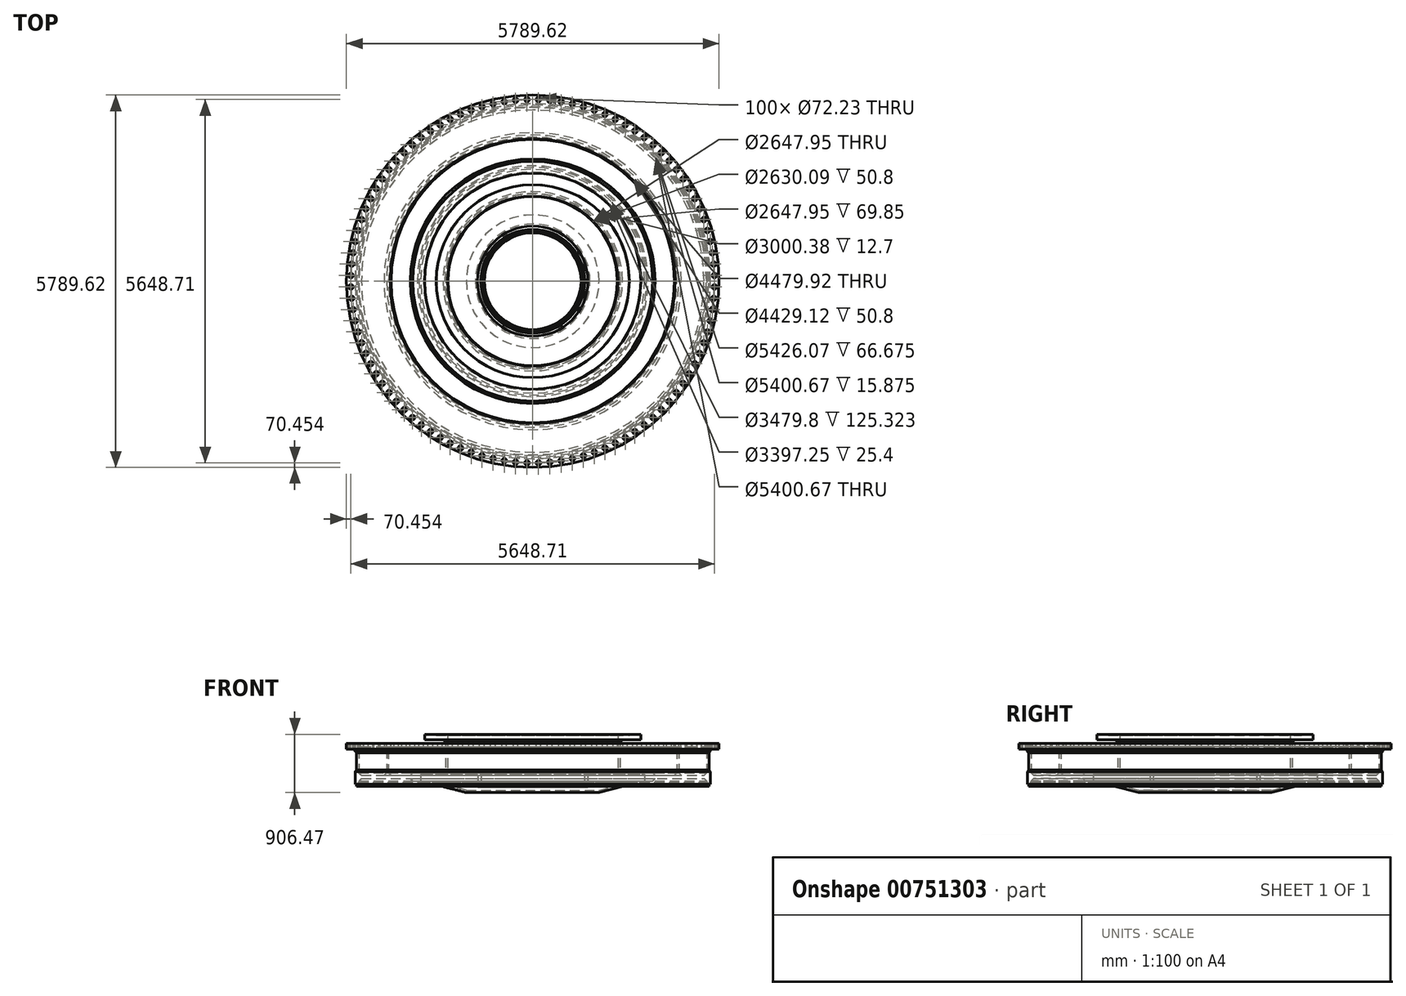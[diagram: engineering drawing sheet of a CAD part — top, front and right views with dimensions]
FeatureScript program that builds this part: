
annotation { "Feature Type Name" : "Feature", "Feature Type Description" : "" }
export const myFeature = defineFeature(function(context is Context, id is Id, definition is map)
    precondition{}
    {
        {
            var Q0;
            Q0=qCreatedBy(makeId("Front.planeOp"),FACE);
            var sketch = newSketch(context, id + "F0", { "sketchPlane" : qUnion([Q0])});
            skLineSegment(sketch, "E0", {"start": v(-1031.08, 176.21) * mm, "end": v(-1498.6, 296.47) * mm});
            skLineSegment(sketch, "E1", {"start": v(-1031.08, 212.27) * mm, "end": v(-1489.9, 330.29) * mm});
            skLineSegment(sketch, "E2", {"start": v(-1498.6, 296.47) * mm, "end": v(-1489.9, 330.29) * mm});
            skLineSegment(sketch, "E3", {"start": v(-751.28, 261.94) * mm, "end": v(-852.49, 261.94) * mm});
            skLineSegment(sketch, "E4", {"start": v(-852.49, 261.94) * mm, "end": v(-852.49, 442.91) * mm});
            skLineSegment(sketch, "E5", {"start": v(-852.49, 442.91) * mm, "end": v(-890.59, 481.01) * mm});
            skLineSegment(sketch, "E6", {"start": v(-890.59, 481.01) * mm, "end": v(-1698.62, 481.01) * mm});
            skLineSegment(sketch, "E7", {"start": v(-751.28, 261.94) * mm, "end": v(-751.28, 325.44) * mm});
            skLineSegment(sketch, "E8", {"start": v(-801.69, 357.19) * mm, "end": v(-801.69, 468.31) * mm});
            skLineSegment(sketch, "E9", {"start": v(-801.69, 468.31) * mm, "end": v(-795.34, 468.31) * mm});
            skLineSegment(sketch, "E10", {"start": v(-795.34, 468.31) * mm, "end": v(-795.34, 493.71) * mm});
            skLineSegment(sketch, "E11", {"start": v(-795.34, 493.71) * mm, "end": v(-808.04, 506.41) * mm});
            skLineSegment(sketch, "E12", {"start": v(-808.04, 506.41) * mm, "end": v(-857.25, 506.41) * mm});
            skLineSegment(sketch, "E13", {"start": v(-857.25, 506.41) * mm, "end": v(-857.25, 519.11) * mm});
            skLineSegment(sketch, "E14", {"start": v(-857.25, 519.11) * mm, "end": v(-1315.05, 519.11) * mm});
            skLineSegment(sketch, "E15", {"start": v(-1031.08, 176.21) * mm, "end": v(-1031.08, 212.27) * mm});
            skLineSegment(sketch, "E16", {"start": v(-751.28, 325.44) * mm, "end": v(-769.94, 325.44) * mm});
            skLineSegment(sketch, "E17", {"start": v(-769.94, 325.44) * mm, "end": v(-801.69, 357.19) * mm});
            skLineSegment(sketch, "E18", {"start": v(-1315.05, 519.11) * mm, "end": v(-1323.98, 528.04) * mm});
            skLineSegment(sketch, "E19", {"start": v(-1323.98, 528.04) * mm, "end": v(-1323.98, 940.4) * mm});
            skLineSegment(sketch, "E20", {"start": v(-1323.98, 940.4) * mm, "end": v(-1315.05, 949.33) * mm});
            skLineSegment(sketch, "E21", {"start": v(-1315.05, 949.33) * mm, "end": v(-1315.05, 1000.13) * mm});
            skLineSegment(sketch, "E22", {"start": v(-1315.05, 1000.13) * mm, "end": v(-1323.98, 1000.13) * mm});
            skLineSegment(sketch, "E23", {"start": v(-1323.98, 1000.13) * mm, "end": v(-1323.98, 1069.98) * mm});
            skLineSegment(sketch, "E24", {"start": v(-1323.98, 1069.98) * mm, "end": v(-1500.19, 1069.98) * mm});
            skLineSegment(sketch, "E25", {"start": v(-1500.19, 1069.98) * mm, "end": v(-1500.19, 1082.68) * mm});
            skLineSegment(sketch, "E26", {"start": v(-1500.19, 1082.68) * mm, "end": v(-1679.58, 1082.68) * mm});
            skLineSegment(sketch, "E27", {"start": v(-1679.58, 1082.68) * mm, "end": v(-1679.58, 1000.12) * mm});
            skLineSegment(sketch, "E28", {"start": v(-1679.58, 1000.13) * mm, "end": v(-2214.56, 892.18) * mm, "construction": true});
            skLineSegment(sketch, "E29", {"start": v(-2214.56, 892.18) * mm, "end": v(-2214.56, 942.97) * mm});
            skLineSegment(sketch, "E30", {"start": v(-2214.56, 942.98) * mm, "end": v(-2894.8, 942.98) * mm});
            skLineSegment(sketch, "E31", {"start": v(-2894.8, 942.97) * mm, "end": v(-2894.8, 854.07) * mm});
            skLineSegment(sketch, "E32", {"start": v(-2763.44, 822.32) * mm, "end": v(-2738.44, 797.32) * mm});
            skLineSegment(sketch, "E33", {"start": v(-2738.44, 797.32) * mm, "end": v(-2738.44, 525.46) * mm});
            skLineSegment(sketch, "E34", {"start": v(-2738.44, 525.46) * mm, "end": v(-2759.87, 504.03) * mm});
            skLineSegment(sketch, "E35", {"start": v(-2759.87, 504.03) * mm, "end": v(-2759.87, 304) * mm});
            skLineSegment(sketch, "E36", {"start": v(-2759.87, 304) * mm, "end": v(-2738.44, 304) * mm});
            skLineSegment(sketch, "E37", {"start": v(-2738.44, 304) * mm, "end": v(-2738.44, 272.26) * mm});
            skLineSegment(sketch, "E38", {"start": v(-2662.24, 392.9) * mm, "end": v(-1901.83, 392.9) * mm});
            skLineSegment(sketch, "E39", {"start": v(-1793.88, 354.8) * mm, "end": v(-1769.36, 330.29) * mm});
            skLineSegment(sketch, "E40", {"start": v(-1769.36, 330.29) * mm, "end": v(-1739.9, 330.29) * mm});
            skLineSegment(sketch, "E41", {"start": v(-1739.9, 330.29) * mm, "end": v(-1739.9, 455.61) * mm});
            skLineSegment(sketch, "E42", {"start": v(-1739.9, 455.61) * mm, "end": v(-1698.62, 455.61) * mm});
            skLineSegment(sketch, "E43", {"start": v(-1698.62, 455.61) * mm, "end": v(-1698.62, 481.01) * mm});
            skLineSegment(sketch, "E44", {"start": v(-2894.8, 854.08) * mm, "end": v(-2763.44, 854.08) * mm});
            skLineSegment(sketch, "E45", {"start": v(-2763.44, 854.07) * mm, "end": v(-2763.44, 822.32) * mm});
            skLineSegment(sketch, "E46", {"start": v(-2700.34, 854.08) * mm, "end": v(-2700.34, 481.8) * mm});
            skLineSegment(sketch, "E47", {"start": v(-2700.34, 481.8) * mm, "end": v(-2662.24, 443.7) * mm});
            skLineSegment(sketch, "E48", {"start": v(-2662.24, 443.7) * mm, "end": v(-2309.81, 443.7) * mm});
            skLineSegment(sketch, "E49", {"start": v(-2309.81, 443.7) * mm, "end": v(-2271.71, 481.8) * mm});
            skLineSegment(sketch, "E50", {"start": v(-2271.71, 481.8) * mm, "end": v(-2271.71, 854.08) * mm});
            skLineSegment(sketch, "E51", {"start": v(-2271.71, 854.08) * mm, "end": v(-2309.81, 892.18) * mm});
            skLineSegment(sketch, "E52", {"start": v(-2309.81, 892.18) * mm, "end": v(-2662.24, 892.18) * mm});
            skLineSegment(sketch, "E53", {"start": v(-2662.24, 892.18) * mm, "end": v(-2700.34, 854.08) * mm});
            skLineSegment(sketch, "E54", {"start": v(-1679.58, 1000.13) * mm, "end": v(-1393.83, 1000.13) * mm});
            skLineSegment(sketch, "E55", {"start": v(-1393.83, 1000.13) * mm, "end": v(-1355.72, 962.02) * mm});
            skLineSegment(sketch, "E56", {"start": v(-1355.73, 962.02) * mm, "end": v(-1355.73, 528.04) * mm});
            skLineSegment(sketch, "E57", {"start": v(-2214.56, 892.18) * mm, "end": v(-2239.96, 848.18) * mm});
            skLineSegment(sketch, "E58", {"start": v(-2239.96, 848.18) * mm, "end": v(-2239.96, 481.8) * mm});
            skLineSegment(sketch, "E59", {"start": v(-2239.96, 481.8) * mm, "end": v(-2201.86, 443.7) * mm});
            skLineSegment(sketch, "E60", {"start": v(-2201.86, 443.7) * mm, "end": v(-1901.83, 443.7) * mm});
            skLineSegment(sketch, "E61", {"start": v(-1901.83, 443.7) * mm, "end": v(-1863.73, 481.8) * mm});
            skLineSegment(sketch, "E62", {"start": v(-1863.73, 481.8) * mm, "end": v(-1863.73, 519.11) * mm});
            skLineSegment(sketch, "E63", {"start": v(-1863.73, 519.11) * mm, "end": v(-1364.65, 519.11) * mm});
            skLineSegment(sketch, "E64", {"start": v(-1364.65, 519.11) * mm, "end": v(-1355.73, 528.04) * mm});
            skLineSegment(sketch, "E65", {"start": v(-1793.88, 354.8) * mm, "end": v(-1863.73, 354.8) * mm});
            skLineSegment(sketch, "E66", {"start": v(0, 0) * mm, "end": v(-2759.87, 0) * mm, "construction": true});
            skLineSegment(sketch, "E67", {"start": v(0, 0) * mm, "end": v(0, 1082.68) * mm, "construction": true});
            skLineSegment(sketch, "E68", {"start": v(-2700.34, 338.93) * mm, "end": v(-2713.04, 338.93) * mm});
            skLineSegment(sketch, "E69", {"start": v(-2713.04, 338.93) * mm, "end": v(-2713.04, 272.26) * mm});
            skLineSegment(sketch, "E70", {"start": v(-2713.04, 272.26) * mm, "end": v(-2738.44, 272.26) * mm});
            skLineSegment(sketch, "E71", {"start": v(-1863.73, 354.8) * mm, "end": v(-1901.83, 392.9) * mm});
            skLineSegment(sketch, "E72", {"start": v(-2700.34, 338.93) * mm, "end": v(-2700.34, 354.8) * mm});
            skLineSegment(sketch, "E73", {"start": v(-2700.34, 354.8) * mm, "end": v(-2662.24, 392.9) * mm});
            skLineSegment(sketch, "E74", {"start": v(-1863.73, 354.8) * mm, "end": v(-2700.34, 354.8) * mm, "construction": true});
            skLineSegment(sketch, "E75", {"start": v(-1489.9, 330.29) * mm, "end": v(-1739.9, 330.29) * mm, "construction": true});
            skLineSegment(sketch, "E76", {"start": v(-1498.6, 296.47) * mm, "end": v(-2713.04, 296.47) * mm, "construction": true});
            skSolve(sketch);
        }
        {
            var Q0;
            Q0 = qSketchRegion(id + "F0", true);
            var Q1;
            Q1=sQuery(id+"F0.wireOp",EDGE,"E67");
            revolve(context, id + "F1", {"surfaceOperationType" : NewSurfaceOperationType.NEW, "entities" : qUnion([Q0]), "axis" : qUnion([Q1]), "revolveType" : RevolveType.FULL});
        }
        {
            var Q0;
            Q0=makeQuery(id+"F1.opRevolve","SWEPT_FACE",FACE,{"disambiguationData":[OSD([sQuery(id+"F0.wireOp",EDGE,"E30")])]});
            var sketch = newSketch(context, id + "F2", { "sketchPlane" : qUnion([Q0])});
            skCircle(sketch, "E77", {"center": v(0, 0) * mm, "radius": 2825.75 * mm, "construction": true});
            skLineSegment(sketch, "E78", {"start": v(-88.76, -2824.36) * mm, "end": v(0, 0) * mm, "construction": true});
            skLineSegment(sketch, "E79", {"start": v(0, 0) * mm, "end": v(0, -2825.75) * mm, "construction": true});
            skCircle(sketch, "E80", {"center": v(-88.76, -2824.36) * mm, "radius": 36.12 * mm});
            skCircle(sketch, "E81.1.0", {"center": v(88.76, -2824.36) * mm, "radius": 36.12 * mm});
            skCircle(sketch, "E81.2.0", {"center": v(265.93, -2813.2) * mm, "radius": 36.12 * mm});
            skCircle(sketch, "E81.3.0", {"center": v(442.04, -2790.96) * mm, "radius": 36.12 * mm});
            skCircle(sketch, "E81.4.0", {"center": v(616.42, -2757.7) * mm, "radius": 36.12 * mm});
            skCircle(sketch, "E81.5.0", {"center": v(788.36, -2713.55) * mm, "radius": 36.12 * mm});
            skCircle(sketch, "E81.6.0", {"center": v(957.19, -2658.7) * mm, "radius": 36.12 * mm});
            skCircle(sketch, "E81.7.0", {"center": v(1122.24, -2593.35) * mm, "radius": 36.12 * mm});
            skCircle(sketch, "E81.8.0", {"center": v(1282.86, -2517.76) * mm, "radius": 36.12 * mm});
            skCircle(sketch, "E81.9.0", {"center": v(1438.42, -2432.24) * mm, "radius": 36.12 * mm});
            skCircle(sketch, "E81.10.0", {"center": v(1588.3, -2337.12) * mm, "radius": 36.12 * mm});
            skCircle(sketch, "E81.11.0", {"center": v(1731.92, -2232.78) * mm, "radius": 36.12 * mm});
            skCircle(sketch, "E81.12.0", {"center": v(1868.7, -2119.63) * mm, "radius": 36.12 * mm});
            skCircle(sketch, "E81.13.0", {"center": v(1998.1, -1998.1) * mm, "radius": 36.12 * mm});
            skCircle(sketch, "E81.14.0", {"center": v(2119.63, -1868.7) * mm, "radius": 36.12 * mm});
            skCircle(sketch, "E81.15.0", {"center": v(2232.78, -1731.92) * mm, "radius": 36.12 * mm});
            skCircle(sketch, "E81.16.0", {"center": v(2337.12, -1588.3) * mm, "radius": 36.12 * mm});
            skCircle(sketch, "E81.17.0", {"center": v(2432.24, -1438.42) * mm, "radius": 36.12 * mm});
            skCircle(sketch, "E81.18.0", {"center": v(2517.76, -1282.86) * mm, "radius": 36.12 * mm});
            skCircle(sketch, "E81.19.0", {"center": v(2593.35, -1122.24) * mm, "radius": 36.12 * mm});
            skCircle(sketch, "E81.20.0", {"center": v(2658.7, -957.19) * mm, "radius": 36.12 * mm});
            skCircle(sketch, "E81.21.0", {"center": v(2713.55, -788.36) * mm, "radius": 36.12 * mm});
            skCircle(sketch, "E81.22.0", {"center": v(2757.7, -616.42) * mm, "radius": 36.12 * mm});
            skCircle(sketch, "E81.23.0", {"center": v(2790.96, -442.04) * mm, "radius": 36.12 * mm});
            skCircle(sketch, "E81.24.0", {"center": v(2813.2, -265.93) * mm, "radius": 36.12 * mm});
            skCircle(sketch, "E81.25.0", {"center": v(2824.36, -88.76) * mm, "radius": 36.12 * mm});
            skCircle(sketch, "E81.26.0", {"center": v(2824.36, 88.76) * mm, "radius": 36.12 * mm});
            skCircle(sketch, "E81.27.0", {"center": v(2813.2, 265.93) * mm, "radius": 36.12 * mm});
            skCircle(sketch, "E81.28.0", {"center": v(2790.96, 442.04) * mm, "radius": 36.12 * mm});
            skCircle(sketch, "E81.29.0", {"center": v(2757.7, 616.42) * mm, "radius": 36.12 * mm});
            skCircle(sketch, "E81.30.0", {"center": v(2713.55, 788.36) * mm, "radius": 36.12 * mm});
            skCircle(sketch, "E81.31.0", {"center": v(2658.7, 957.19) * mm, "radius": 36.12 * mm});
            skCircle(sketch, "E81.32.0", {"center": v(2593.35, 1122.24) * mm, "radius": 36.12 * mm});
            skCircle(sketch, "E81.33.0", {"center": v(2517.76, 1282.86) * mm, "radius": 36.12 * mm});
            skCircle(sketch, "E81.34.0", {"center": v(2432.24, 1438.42) * mm, "radius": 36.12 * mm});
            skCircle(sketch, "E81.35.0", {"center": v(2337.12, 1588.3) * mm, "radius": 36.12 * mm});
            skCircle(sketch, "E81.36.0", {"center": v(2232.78, 1731.92) * mm, "radius": 36.12 * mm});
            skCircle(sketch, "E81.37.0", {"center": v(2119.63, 1868.7) * mm, "radius": 36.12 * mm});
            skCircle(sketch, "E81.38.0", {"center": v(1998.1, 1998.1) * mm, "radius": 36.12 * mm});
            skCircle(sketch, "E81.39.0", {"center": v(1868.7, 2119.63) * mm, "radius": 36.12 * mm});
            skCircle(sketch, "E81.40.0", {"center": v(1731.92, 2232.78) * mm, "radius": 36.12 * mm});
            skCircle(sketch, "E81.41.0", {"center": v(1588.3, 2337.12) * mm, "radius": 36.12 * mm});
            skCircle(sketch, "E81.42.0", {"center": v(1438.42, 2432.24) * mm, "radius": 36.12 * mm});
            skCircle(sketch, "E81.43.0", {"center": v(1282.86, 2517.76) * mm, "radius": 36.12 * mm});
            skCircle(sketch, "E81.44.0", {"center": v(1122.24, 2593.35) * mm, "radius": 36.12 * mm});
            skCircle(sketch, "E81.45.0", {"center": v(957.19, 2658.7) * mm, "radius": 36.12 * mm});
            skCircle(sketch, "E81.46.0", {"center": v(788.36, 2713.55) * mm, "radius": 36.12 * mm});
            skCircle(sketch, "E81.47.0", {"center": v(616.42, 2757.7) * mm, "radius": 36.12 * mm});
            skCircle(sketch, "E81.48.0", {"center": v(442.04, 2790.96) * mm, "radius": 36.12 * mm});
            skCircle(sketch, "E81.49.0", {"center": v(265.93, 2813.2) * mm, "radius": 36.12 * mm});
            skCircle(sketch, "E81.50.0", {"center": v(88.76, 2824.36) * mm, "radius": 36.12 * mm});
            skCircle(sketch, "E81.51.0", {"center": v(-88.76, 2824.36) * mm, "radius": 36.12 * mm});
            skCircle(sketch, "E81.52.0", {"center": v(-265.93, 2813.2) * mm, "radius": 36.12 * mm});
            skCircle(sketch, "E81.53.0", {"center": v(-442.04, 2790.96) * mm, "radius": 36.12 * mm});
            skCircle(sketch, "E81.54.0", {"center": v(-616.42, 2757.7) * mm, "radius": 36.12 * mm});
            skCircle(sketch, "E81.55.0", {"center": v(-788.36, 2713.55) * mm, "radius": 36.12 * mm});
            skCircle(sketch, "E81.56.0", {"center": v(-957.19, 2658.7) * mm, "radius": 36.12 * mm});
            skCircle(sketch, "E81.57.0", {"center": v(-1122.24, 2593.35) * mm, "radius": 36.12 * mm});
            skCircle(sketch, "E81.58.0", {"center": v(-1282.86, 2517.76) * mm, "radius": 36.12 * mm});
            skCircle(sketch, "E81.59.0", {"center": v(-1438.42, 2432.24) * mm, "radius": 36.12 * mm});
            skCircle(sketch, "E81.60.0", {"center": v(-1588.3, 2337.12) * mm, "radius": 36.12 * mm});
            skCircle(sketch, "E81.61.0", {"center": v(-1731.92, 2232.78) * mm, "radius": 36.12 * mm});
            skCircle(sketch, "E81.62.0", {"center": v(-1868.7, 2119.63) * mm, "radius": 36.12 * mm});
            skCircle(sketch, "E81.63.0", {"center": v(-1998.1, 1998.1) * mm, "radius": 36.12 * mm});
            skCircle(sketch, "E81.64.0", {"center": v(-2119.63, 1868.7) * mm, "radius": 36.12 * mm});
            skCircle(sketch, "E81.65.0", {"center": v(-2232.78, 1731.92) * mm, "radius": 36.12 * mm});
            skCircle(sketch, "E81.66.0", {"center": v(-2337.12, 1588.3) * mm, "radius": 36.12 * mm});
            skCircle(sketch, "E81.67.0", {"center": v(-2432.24, 1438.42) * mm, "radius": 36.12 * mm});
            skCircle(sketch, "E81.68.0", {"center": v(-2517.76, 1282.86) * mm, "radius": 36.12 * mm});
            skCircle(sketch, "E81.69.0", {"center": v(-2593.35, 1122.24) * mm, "radius": 36.12 * mm});
            skCircle(sketch, "E81.70.0", {"center": v(-2658.7, 957.19) * mm, "radius": 36.12 * mm});
            skCircle(sketch, "E81.71.0", {"center": v(-2713.55, 788.36) * mm, "radius": 36.12 * mm});
            skCircle(sketch, "E81.72.0", {"center": v(-2757.7, 616.42) * mm, "radius": 36.12 * mm});
            skCircle(sketch, "E81.73.0", {"center": v(-2790.96, 442.04) * mm, "radius": 36.12 * mm});
            skCircle(sketch, "E81.74.0", {"center": v(-2813.2, 265.93) * mm, "radius": 36.12 * mm});
            skCircle(sketch, "E81.75.0", {"center": v(-2824.36, 88.76) * mm, "radius": 36.12 * mm});
            skCircle(sketch, "E81.76.0", {"center": v(-2824.36, -88.76) * mm, "radius": 36.12 * mm});
            skCircle(sketch, "E81.77.0", {"center": v(-2813.2, -265.93) * mm, "radius": 36.12 * mm});
            skCircle(sketch, "E81.78.0", {"center": v(-2790.96, -442.04) * mm, "radius": 36.12 * mm});
            skCircle(sketch, "E81.79.0", {"center": v(-2757.7, -616.42) * mm, "radius": 36.12 * mm});
            skCircle(sketch, "E81.80.0", {"center": v(-2713.55, -788.36) * mm, "radius": 36.12 * mm});
            skCircle(sketch, "E81.81.0", {"center": v(-2658.7, -957.19) * mm, "radius": 36.12 * mm});
            skCircle(sketch, "E81.82.0", {"center": v(-2593.35, -1122.24) * mm, "radius": 36.12 * mm});
            skCircle(sketch, "E81.83.0", {"center": v(-2517.76, -1282.86) * mm, "radius": 36.12 * mm});
            skCircle(sketch, "E81.84.0", {"center": v(-2432.24, -1438.42) * mm, "radius": 36.12 * mm});
            skCircle(sketch, "E81.85.0", {"center": v(-2337.12, -1588.3) * mm, "radius": 36.12 * mm});
            skCircle(sketch, "E81.86.0", {"center": v(-2232.78, -1731.92) * mm, "radius": 36.12 * mm});
            skCircle(sketch, "E81.87.0", {"center": v(-2119.63, -1868.7) * mm, "radius": 36.12 * mm});
            skCircle(sketch, "E81.88.0", {"center": v(-1998.1, -1998.1) * mm, "radius": 36.12 * mm});
            skCircle(sketch, "E81.89.0", {"center": v(-1868.7, -2119.63) * mm, "radius": 36.12 * mm});
            skCircle(sketch, "E81.90.0", {"center": v(-1731.92, -2232.78) * mm, "radius": 36.12 * mm});
            skCircle(sketch, "E81.91.0", {"center": v(-1588.3, -2337.12) * mm, "radius": 36.12 * mm});
            skCircle(sketch, "E81.92.0", {"center": v(-1438.42, -2432.24) * mm, "radius": 36.12 * mm});
            skCircle(sketch, "E81.93.0", {"center": v(-1282.86, -2517.76) * mm, "radius": 36.12 * mm});
            skCircle(sketch, "E81.94.0", {"center": v(-1122.24, -2593.35) * mm, "radius": 36.12 * mm});
            skCircle(sketch, "E81.95.0", {"center": v(-957.19, -2658.7) * mm, "radius": 36.12 * mm});
            skCircle(sketch, "E81.96.0", {"center": v(-788.36, -2713.55) * mm, "radius": 36.12 * mm});
            skCircle(sketch, "E81.97.0", {"center": v(-616.42, -2757.7) * mm, "radius": 36.12 * mm});
            skCircle(sketch, "E81.98.0", {"center": v(-442.04, -2790.96) * mm, "radius": 36.12 * mm});
            skCircle(sketch, "E81.99.0", {"center": v(-265.93, -2813.2) * mm, "radius": 36.12 * mm});
            skSolve(sketch);
        }
        {
            var Q0;
            Q0 = qSketchRegion(id + "F2", true);
            extrude(context, id + "F3", {"entities" : qUnion([Q0]), "operationType" : NewBodyOperationType.REMOVE, "endBound" : BoundingType.UP_TO_NEXT, "oppositeDirection" : true, "depth" : 25.4 * mm, "offsetDistance" : 25.4 * mm});
        }
    });
